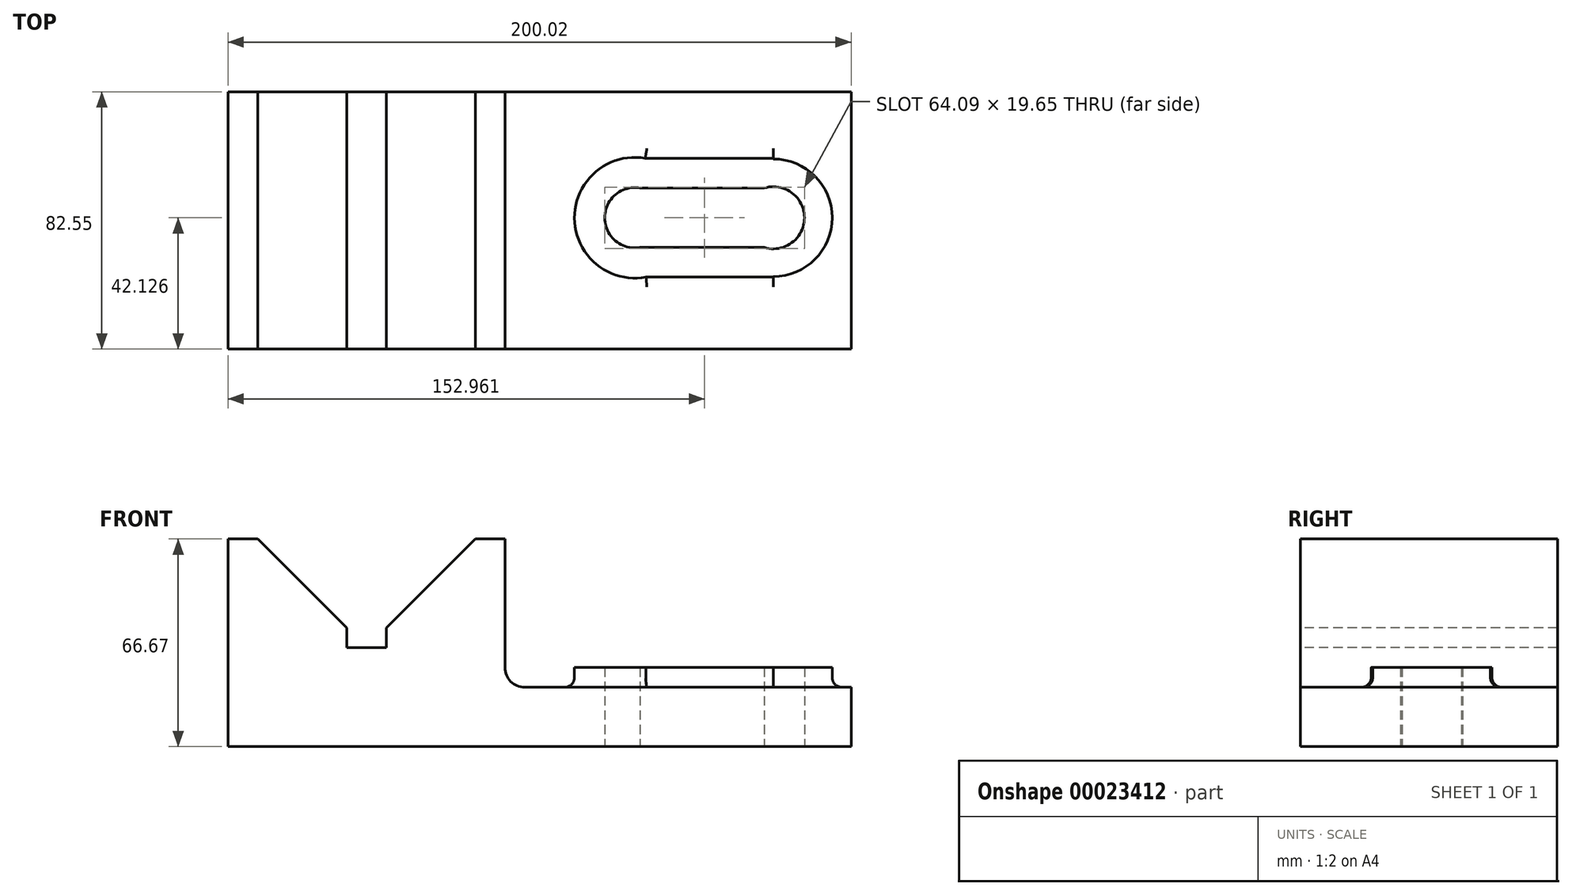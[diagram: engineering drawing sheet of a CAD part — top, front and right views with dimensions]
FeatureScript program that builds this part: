
annotation { "Feature Type Name" : "Feature", "Feature Type Description" : "" }
export const myFeature = defineFeature(function(context is Context, id is Id, definition is map)
    precondition{}
    {
        {
            var Q0;
            Q0=qCreatedBy(makeId("Front.planeOp"),FACE);
            var sketch = newSketch(context, id + "F0", { "sketchPlane" : qUnion([Q0])});
            skLineSegment(sketch, "E0", {"start": v(-53.01, -34.5) * mm, "end": v(-53.01, 32.17) * mm});
            skLineSegment(sketch, "E1", {"start": v(-53.01, 32.17) * mm, "end": v(-43.49, 32.17) * mm});
            skLineSegment(sketch, "E2", {"start": v(26.36, 32.17) * mm, "end": v(35.89, 32.17) * mm});
            skLineSegment(sketch, "E3", {"start": v(35.89, 32.17) * mm, "end": v(35.89, -34.5) * mm});
            skLineSegment(sketch, "E4", {"start": v(-43.49, 32.17) * mm, "end": v(-14.91, 3.6) * mm});
            skLineSegment(sketch, "E5", {"start": v(-14.91, 3.6) * mm, "end": v(-14.91, -2.75) * mm});
            skLineSegment(sketch, "E6", {"start": v(-14.91, -2.75) * mm, "end": v(-2.21, -2.75) * mm});
            skLineSegment(sketch, "E7", {"start": v(-2.21, -2.75) * mm, "end": v(-2.21, 3.6) * mm});
            skLineSegment(sketch, "E8", {"start": v(-2.21, 3.6) * mm, "end": v(26.36, 32.17) * mm});
            skLineSegment(sketch, "E9", {"start": v(-53.01, -34.5) * mm, "end": v(147.01, -34.5) * mm});
            skLineSegment(sketch, "E10", {"start": v(147.01, -34.5) * mm, "end": v(147.01, -15.45) * mm});
            skLineSegment(sketch, "E11", {"start": v(147.01, -15.45) * mm, "end": v(35.89, -15.45) * mm});
            skSolve(sketch);
        }
        {
            var Q0;
            {var subQ3=sQuery(id+"F0.wireOp",EDGE,"E0");Q0=makeQuery(id+"F0.imprint","IMPRINT",FACE,{"disambiguationData":[TD([[makeQuery(id+"F0.imprint","IMPRINT",EDGE,{"derivedFrom":subQ3}),-1.0]])]});}
            var Q1;
            {var subQ1=sQuery(id+"F0.wireOp",EDGE,"E10");Q1=makeQuery(id+"F0.imprint","IMPRINT",FACE,{"disambiguationData":[TD([[makeQuery(id+"F0.imprint","IMPRINT",EDGE,{"derivedFrom":subQ1}),1.0]])]});}
            extrude(context, id + "F1", {"entities" : qUnion([Q0, Q1]), "oppositeDirection" : true, "depth" : 82.55 * mm});
        }
        {
            var Q0;
            Q0=makeQuery(id+"F1.opExtrude","SWEPT_EDGE",EDGE,{"disambiguationData":[OSD([sQuery(id+"F0.wireOp",EDGE,"E3"),sQuery(id+"F0.wireOp",EDGE,"E11")])]});
            fillet(context, id + "F2", {"entities" : qUnion([Q0]), "radius" : 6.35 * mm, "tangentPropagation" : true, "allowEdgeOverflow" : false});
        }
        {
            var Q0;
            Q0=makeQuery(id+"F1.opExtrude","SWEPT_FACE",FACE,{"disambiguationData":[OSD([sQuery(id+"F0.wireOp",EDGE,"E11")])]});
            var sketch = newSketch(context, id + "F3", { "sketchPlane" : qUnion([Q0])});
            skLineSegment(sketch, "E12.bottom", {"start": v(77.58, 51.65) * mm, "end": v(122.03, 51.65) * mm});
            skLineSegment(sketch, "E12.top", {"start": v(77.58, 32.6) * mm, "end": v(122.03, 32.6) * mm});
            skLineSegment(sketch, "E13.bottom", {"start": v(77.41, 61.18) * mm, "end": v(122.03, 61.18) * mm});
            skLineSegment(sketch, "E13.top", {"start": v(77.58, 23.08) * mm, "end": v(122.03, 23.08) * mm});
            skPoint(sketch, "E14.start.orphan", {"position": v(122.03, 42.13) * mm});
            skLineSegment(sketch, "E15", {"start": v(122.03, 61.18) * mm, "end": v(122.03, 61) * mm});
            skArc(sketch, "E16", {"start": v(81.16, 61.18) * mm, "mid": v(58.2, 42.13) * mm, "end": v(81.16, 23.08) * mm});
            skArc(sketch, "E17", {"start": v(122.03, 23.26) * mm, "mid": v(140.9, 42.13) * mm, "end": v(122.03, 61) * mm});
            skArc(sketch, "E18", {"start": v(79.29, 51.65) * mm, "mid": v(67.9, 42.13) * mm, "end": v(79.29, 32.6) * mm});
            skArc(sketch, "E19", {"start": v(119.1, 32.6) * mm, "mid": v(132, 42.13) * mm, "end": v(119.1, 51.65) * mm});
            skPoint(sketch, "E20.orphan", {"position": v(99.8, 51.65) * mm});
            skPoint(sketch, "E21.end.orphan", {"position": v(99.8, 32.6) * mm});
            skLineSegment(sketch, "E22.trimOffspring", {"start": v(122.03, 52.1) * mm, "end": v(122.03, 51.65) * mm});
            skLineSegment(sketch, "E23.trimOffspring", {"start": v(122.03, 32.6) * mm, "end": v(122.03, 32.16) * mm});
            skLineSegment(sketch, "E24.trimOffspring", {"start": v(122.03, 23.26) * mm, "end": v(122.03, 23.08) * mm});
            skSolve(sketch);
        }
        {
            var Q0;
            {var subQ9=sQuery(id+"F3.wireOp",EDGE,"E15");Q0=makeQuery(id+"F3.imprint","IMPRINT",FACE,{"disambiguationData":[TD([[makeQuery(id+"F3.imprint","IMPRINT",EDGE,{"derivedFrom":subQ9}),-1.0]])]});}
            extrude(context, id + "F4", {"entities" : qUnion([Q0]), "operationType" : NewBodyOperationType.ADD, "depth" : 6.35 * mm});
        }
        {
            var Q0;
            Q0=makeQuery(id+"F4.opExtrude","CAP_EDGE",EDGE,{"disambiguationData":[OSD([sQuery(id+"F3.wireOp",EDGE,"E17")])],"isStart":true});
            fillet(context, id + "F5", {"entities" : qUnion([Q0]), "radius" : 3.17 * mm, "tangentPropagation" : true, "allowEdgeOverflow" : false});
        }
        {
            var Q0;
            Q0=makeQuery(id+"F4.opExtrude","CAP_EDGE",EDGE,{"disambiguationData":[OSD([sQuery(id+"F3.wireOp",EDGE,"E13.top")])],"isStart":true});
            var Q1;
            Q1=makeQuery(id+"F4.opExtrude","CAP_EDGE",EDGE,{"disambiguationData":[OSD([sQuery(id+"F3.wireOp",EDGE,"E16")])],"isStart":true});
            fillet(context, id + "F6", {"entities" : qUnion([Q0, Q1]), "radius" : 3.17 * mm, "tangentPropagation" : true, "allowEdgeOverflow" : false});
        }
        {
            var Q0;
            Q0=makeQuery(id+"F4.opExtrude","CAP_EDGE",EDGE,{"disambiguationData":[OSD([sQuery(id+"F3.wireOp",EDGE,"E13.bottom")])],"isStart":true});
            fillet(context, id + "F7", {"entities" : qUnion([Q0]), "radius" : 3.17 * mm, "tangentPropagation" : true, "allowEdgeOverflow" : false});
        }
        {
            var Q0;
            Q0 = qSketchRegion(id + "F3", true);
            extrude(context, id + "F8", {"entities" : qUnion([Q0]), "operationType" : NewBodyOperationType.ADD, "oppositeDirection" : true, "depth" : 6.35 * mm});
        }
        {
            var Q0;
            Q0=makeQuery(id+"F4.boolean.opBoolean","SPLIT",FACE,{"disambiguationData":[TD([makeQuery(id+"F4.opExtrude","SWEPT_FACE",FACE,{"disambiguationData":[OSD([sQuery(id+"F3.wireOp",EDGE,"E12.bottom")])]})])],"derivedFrom":makeQuery(id+"F1.opExtrude","SWEPT_FACE",FACE,{"disambiguationData":[OSD([sQuery(id+"F0.wireOp",EDGE,"E11")])]})});
            extrude(context, id + "F9", {"entities" : qUnion([Q0]), "operationType" : NewBodyOperationType.REMOVE, "endBound" : BoundingType.THROUGH_ALL, "oppositeDirection" : true, "depth" : 25.4 * mm});
        }
    });
